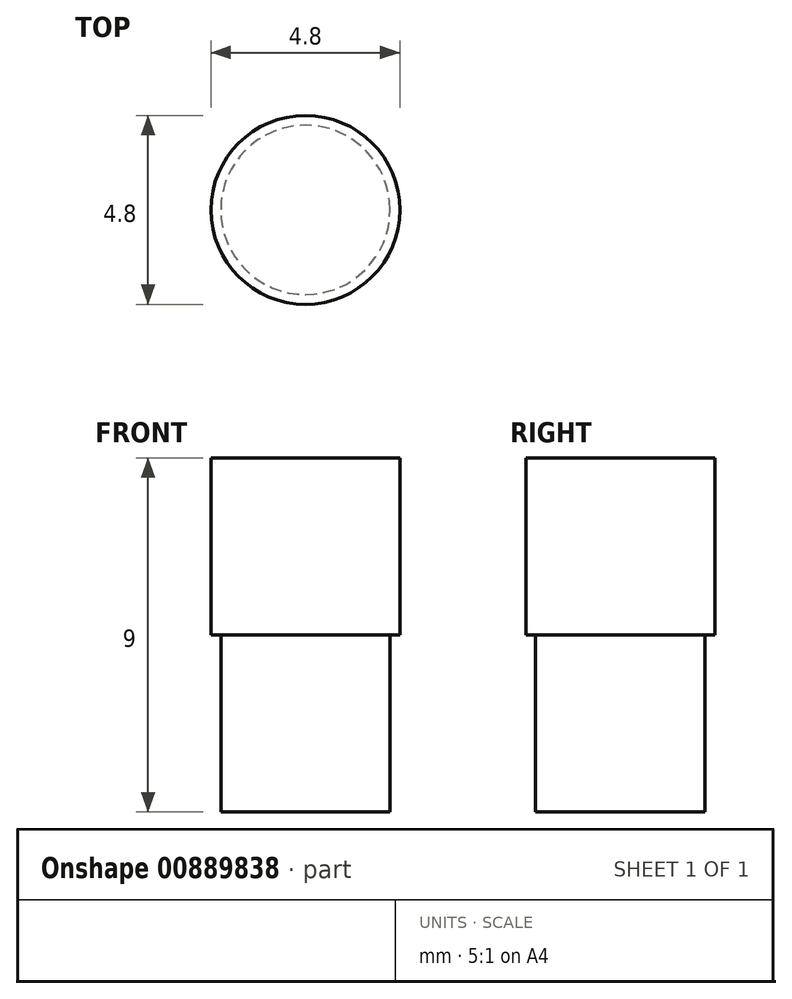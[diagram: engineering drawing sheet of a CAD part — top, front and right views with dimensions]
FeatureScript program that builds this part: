
annotation { "Feature Type Name" : "Feature", "Feature Type Description" : "" }
export const myFeature = defineFeature(function(context is Context, id is Id, definition is map)
    precondition{}
    {
        {
            var Q0;
            Q0=qCreatedBy(makeId("Top.planeOp"),FACE);
            var sketch = newSketch(context, id + "F0", { "sketchPlane" : qUnion([Q0])});
            skCircle(sketch, "E0", {"center": v(0, 0) * mm, "radius": 2.4 * mm});
            skSolve(sketch);
        }
        {
            var Q0;
            Q0=qCreatedBy(makeId("Top.planeOp"),FACE);
            var sketch = newSketch(context, id + "F1", { "sketchPlane" : qUnion([Q0])});
            skCircle(sketch, "E1", {"center": v(0, 0) * mm, "radius": 2.15 * mm});
            skSolve(sketch);
        }
        {
            var Q0;
            Q0 = qSketchRegion(id + "F0", true);
            extrude(context, id + "F2", {"entities" : qUnion([Q0]), "depth" : 4.5 * mm, "offsetDistance" : 25 * mm});
        }
        {
            var Q0;
            Q0 = qSketchRegion(id + "F1", true);
            extrude(context, id + "F3", {"entities" : qUnion([Q0]), "operationType" : NewBodyOperationType.ADD, "oppositeDirection" : true, "depth" : 4.5 * mm, "offsetDistance" : 25 * mm});
        }
    });
